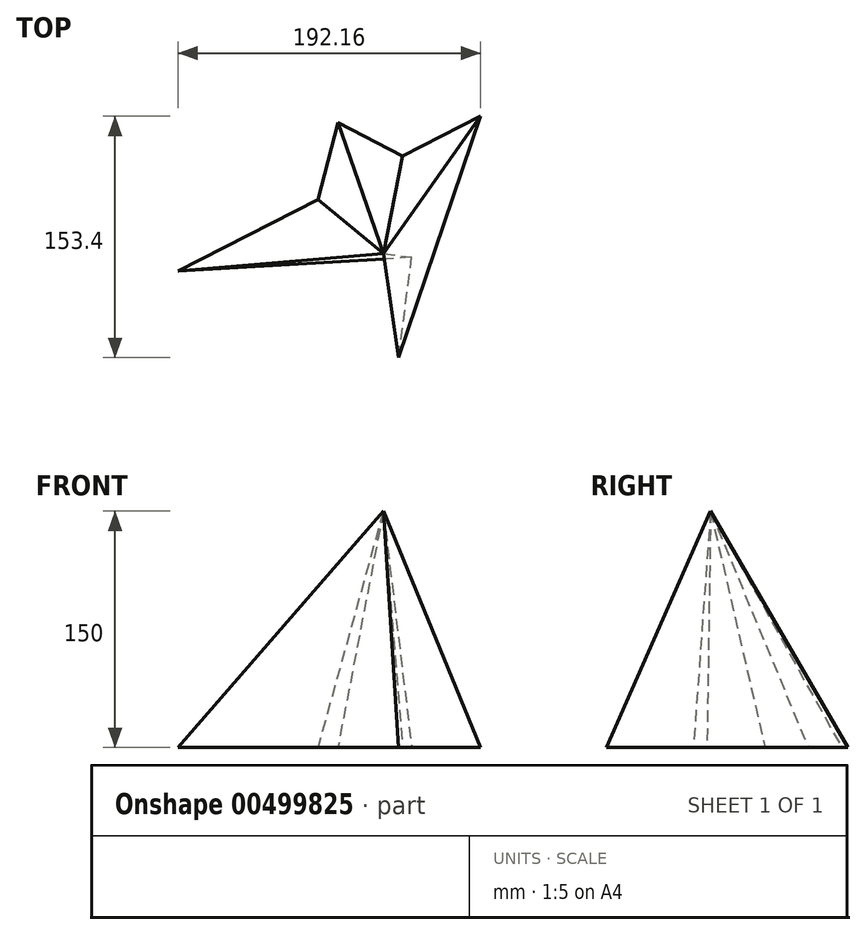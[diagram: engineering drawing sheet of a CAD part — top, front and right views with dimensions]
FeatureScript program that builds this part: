
annotation { "Feature Type Name" : "Feature", "Feature Type Description" : "" }
export const myFeature = defineFeature(function(context is Context, id is Id, definition is map)
    precondition{}
    {
        {
            var Q0;
            Q0=qCreatedBy(makeId("Top.planeOp"),FACE);
            var sketch = newSketch(context, id + "F0", { "sketchPlane" : qUnion([Q0])});
            skLineSegment(sketch, "E0.0", {"start": v(61.85, 87.36) * mm, "end": v(9.82, -66.04) * mm});
            skLineSegment(sketch, "E0.1", {"start": v(9.82, -66.04) * mm, "end": v(18.03, -2.27) * mm});
            skLineSegment(sketch, "E0.2", {"start": v(18.03, -2.27) * mm, "end": v(-130.31, -10.89) * mm});
            skLineSegment(sketch, "E1", {"start": v(-41.51, 34.51) * mm, "end": v(-28.81, 83.2) * mm});
            skLineSegment(sketch, "E2", {"start": v(-28.81, 83.2) * mm, "end": v(12.26, 62) * mm});
            skLineSegment(sketch, "E3", {"start": v(-130.31, -10.89) * mm, "end": v(-41.51, 34.51) * mm});
            skLineSegment(sketch, "E4", {"start": v(12.26, 62) * mm, "end": v(61.85, 87.36) * mm});
            skSolve(sketch);
        }
        {
            var Q0;
            Q0=qCreatedBy(makeId("Top.planeOp"),FACE);
            cPlane(context, id + "F1", {"entities" : qUnion([Q0]), "cplaneType" : CPlaneType.OFFSET, "offset" : 150 * mm, "width" : 150 * mm, "height" : 150 * mm});
        }
        {
            var Q0;
            Q0=qCreatedBy(id+"F1.planeOp",FACE);
            var sketch = newSketch(context, id + "F2", { "sketchPlane" : qUnion([Q0])});
            skPoint(sketch, "E5", {"position": v(0, 0) * mm});
            skSolve(sketch);
        }
        {
            var Q0;
            Q0=sQuery(id+"F2.wireOp",VERTEX,"E5");
            var Q1;
            Q1=makeQuery(id+"F0.imprint","IMPRINT",FACE,{"disambiguationData":[TD([[makeQuery(id+"F0.imprint","IMPRINT",EDGE,{"derivedFrom":sQuery(id+"F0.wireOp",EDGE,"E0.0")}),-1.0]])]});
            loft(context, id + "F3", {"sheetProfilesArray" : [{ "sheetProfileEntities" : qUnion([Q0]) }, { "sheetProfileEntities" : qUnion([Q1]) }]});
        }
    });
